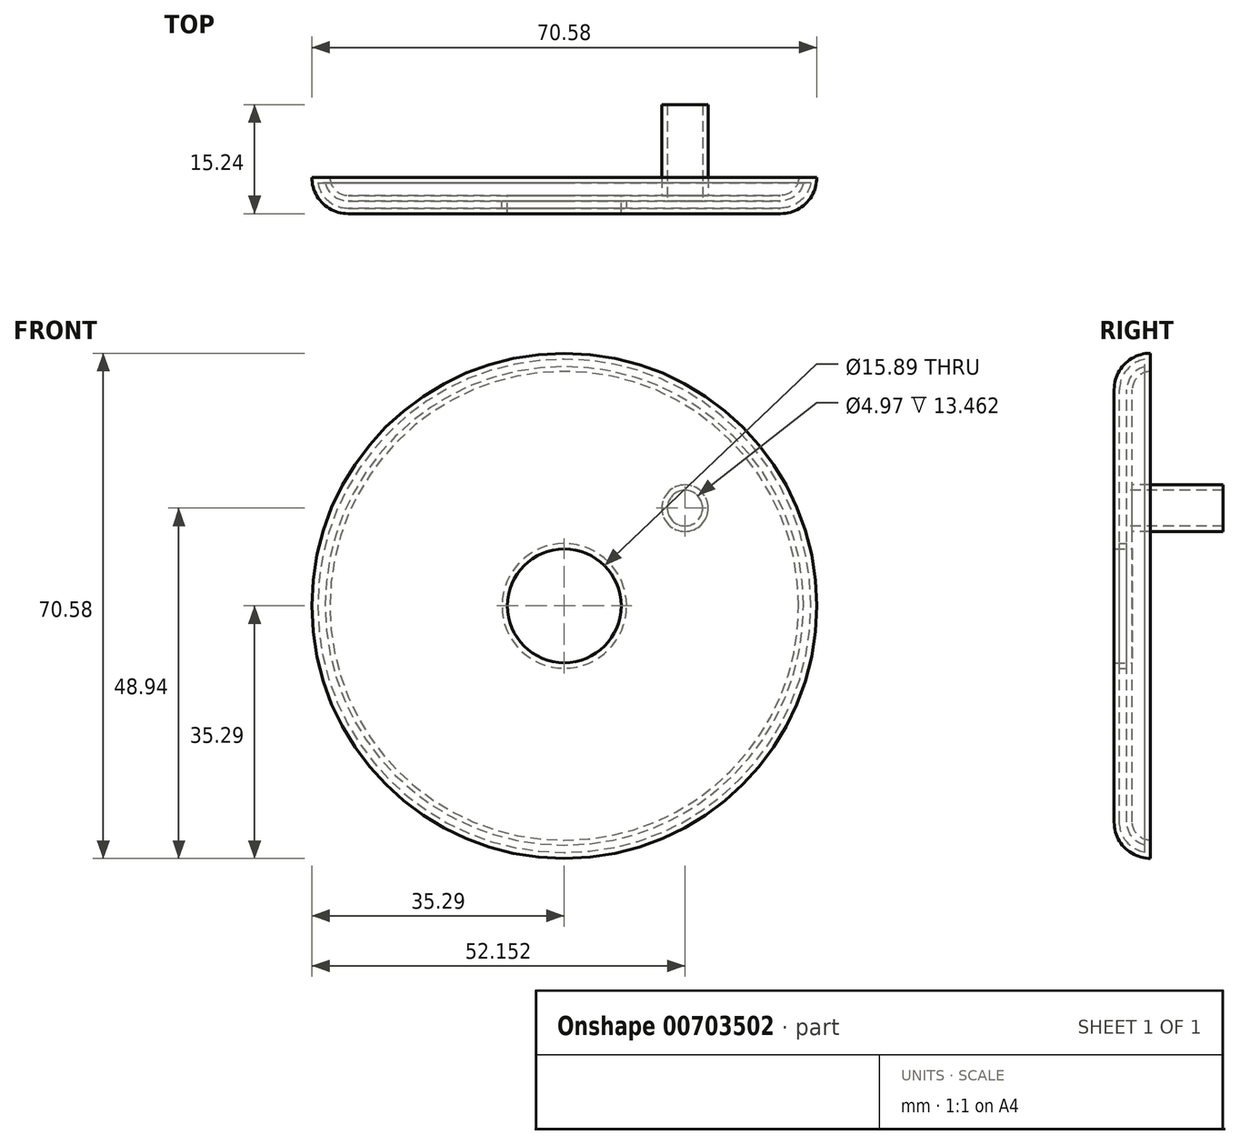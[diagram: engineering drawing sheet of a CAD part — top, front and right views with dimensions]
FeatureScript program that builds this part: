
annotation { "Feature Type Name" : "Feature", "Feature Type Description" : "" }
export const myFeature = defineFeature(function(context is Context, id is Id, definition is map)
    precondition{}
    {
        {
            var Q0;
            Q0=qCreatedBy(makeId("Front.planeOp"),FACE);
            var sketch = newSketch(context, id + "F0", { "sketchPlane" : qUnion([Q0])});
            skCircle(sketch, "E0", {"center": v(0, 0) * mm, "radius": 35.29 * mm});
            skSolve(sketch);
        }
        {
            var Q0;
            Q0=makeQuery(id+"F0.imprint","IMPRINT",FACE,{"disambiguationData":[TD([[makeQuery(id+"F0.imprint","IMPRINT",EDGE,{"derivedFrom":sQuery(id+"F0.wireOp",EDGE,"E0")}),1.0]])]});
            extrude(context, id + "F1", {"entities" : qUnion([Q0]), "depth" : 5.08 * mm, "offsetDistance" : 25.4 * mm});
        }
        {
            var Q0;
            Q0=makeQuery(id+"F1.opExtrude","CAP_FACE",FACE,{"disambiguationData":[OSD([sQuery(id+"F0.wireOp",EDGE,"E0")])],"isStart":false});
            fillet(context, id + "F2", {"entities" : qUnion([Q0]), "radius" : 5.08 * mm, "tangentPropagation" : true, "allowEdgeOverflow" : false});
        }
        {
            var Q0;
            Q0=makeQuery(id+"F1.opExtrude","CAP_FACE",FACE,{"disambiguationData":[OSD([sQuery(id+"F0.wireOp",EDGE,"E0")])],"isStart":true});
            shell(context, id + "F3", {"entities" : qUnion([Q0]), "thickness" : 2.54 * mm});
        }
        {
            var Q0;
            {var subQ0=sQuery(id+"F0.wireOp",EDGE,"E0");Q0=makeQuery(id+"F3.opShell","OFFSET_FACE",FACE,{"disambiguationData":[OSD([subQ0]),TDD([makeQuery(id+"F1.opExtrude","CAP_FACE",FACE,{"disambiguationData":[OSD([subQ0])],"isStart":false})])]});}
            var sketch = newSketch(context, id + "F4", { "sketchPlane" : qUnion([Q0])});
            skCircle(sketch, "E1", {"center": v(0, 0) * mm, "radius": 7.94 * mm});
            skSolve(sketch);
        }
        {
            var Q0;
            Q0 = qSketchRegion(id + "F4", true);
            extrude(context, id + "F5", {"entities" : qUnion([Q0]), "operationType" : NewBodyOperationType.REMOVE, "oppositeDirection" : true, "depth" : 25.4 * mm, "offsetDistance" : 25.4 * mm});
        }
        {
            var Q0;
            {var subQ0=sQuery(id+"F0.wireOp",EDGE,"E0");Q0=makeQuery(id+"F3.opShell","OFFSET_FACE",FACE,{"disambiguationData":[OSD([subQ0]),TDD([makeQuery(id+"F1.opExtrude","CAP_FACE",FACE,{"disambiguationData":[OSD([subQ0])],"isStart":false})])]});}
            var sketch = newSketch(context, id + "F6", { "sketchPlane" : qUnion([Q0])});
            skCircle(sketch, "E2", {"center": v(-16.86, 13.65) * mm, "radius": 3.25 * mm});
            skSolve(sketch);
        }
        {
            var Q0;
            Q0 = qSketchRegion(id + "F6", true);
            extrude(context, id + "F7", {"entities" : qUnion([Q0]), "operationType" : NewBodyOperationType.ADD, "depth" : 12.7 * mm, "offsetDistance" : 25.4 * mm});
        }
        {
            var Q0;
            Q0=makeQuery(id+"F7.opExtrude","CAP_FACE",FACE,{"disambiguationData":[OSD([sQuery(id+"F6.wireOp",EDGE,"E2")])],"isStart":false});
            shell(context, id + "F8", {"entities" : qUnion([Q0]), "thickness" : 0.76 * mm});
        }
    });
